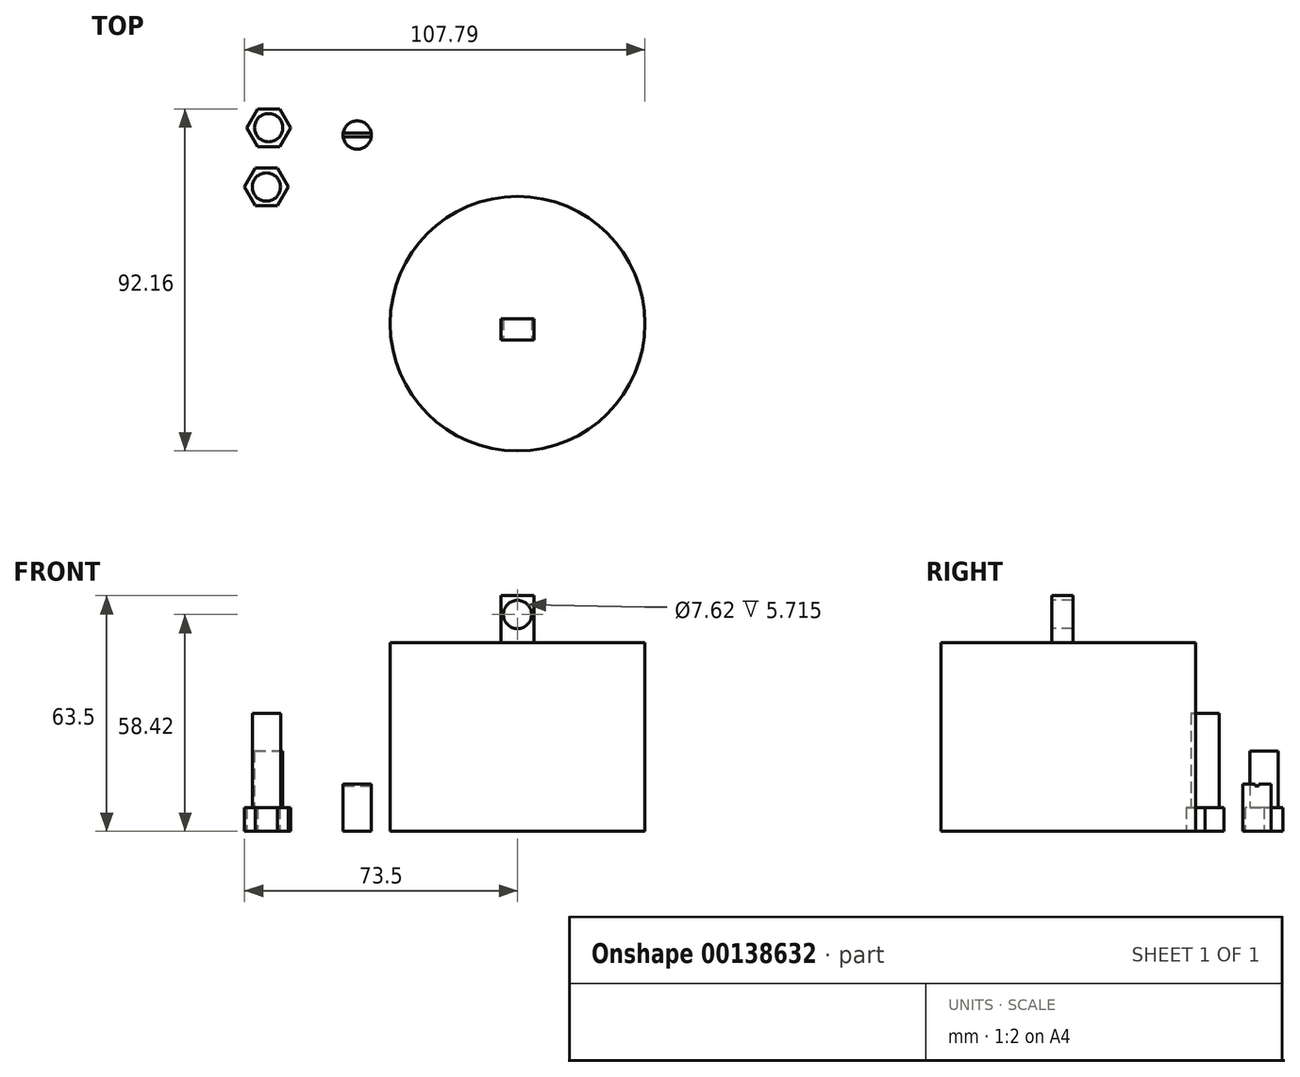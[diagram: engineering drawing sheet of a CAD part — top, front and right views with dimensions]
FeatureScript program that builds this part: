
annotation { "Feature Type Name" : "Feature", "Feature Type Description" : "" }
export const myFeature = defineFeature(function(context is Context, id is Id, definition is map)
    precondition{}
    {
        {
            var Q0;
            Q0=qCreatedBy(makeId("Top.planeOp"),FACE);
            var sketch = newSketch(context, id + "F0", { "sketchPlane" : qUnion([Q0])});
            skCircle(sketch, "E0", {"center": v(0, 0) * mm, "radius": 34.3 * mm});
            skSolve(sketch);
        }
        {
            var Q0;
            Q0 = qSketchRegion(id + "F0", true);
            extrude(context, id + "F1", {"entities" : qUnion([Q0]), "depth" : 50.8 * mm});
        }
        {
            var Q0;
            Q0=makeQuery(id+"F1.opExtrude","CAP_FACE",FACE,{"disambiguationData":[OSD([sQuery(id+"F0.wireOp",EDGE,"E0")])],"isStart":false});
            var sketch = newSketch(context, id + "F2", { "sketchPlane" : qUnion([Q0])});
            skLineSegment(sketch, "E1.top", {"start": v(-4.44, -4.45) * mm, "end": v(4.45, -4.45) * mm});
            skLineSegment(sketch, "E1.left", {"start": v(-4.45, 1.27) * mm, "end": v(-4.45, -4.45) * mm});
            skLineSegment(sketch, "E1.right", {"start": v(4.45, 1.27) * mm, "end": v(4.45, -4.45) * mm});
            skLineSegment(sketch, "E2", {"start": v(4.45, 1.27) * mm, "end": v(-4.45, 1.27) * mm});
            skSolve(sketch);
        }
        {
            var Q0;
            Q0 = qSketchRegion(id + "F2", true);
            extrude(context, id + "F3", {"entities" : qUnion([Q0]), "operationType" : NewBodyOperationType.ADD, "depth" : 12.7 * mm});
        }
        {
            var Q0;
            Q0=makeQuery(id+"F3.opExtrude","SWEPT_FACE",FACE,{"disambiguationData":[OSD([sQuery(id+"F2.wireOp",EDGE,"E1.top")])]});
            var sketch = newSketch(context, id + "F4", { "sketchPlane" : qUnion([Q0])});
            skCircle(sketch, "E3", {"center": v(0, 58.42) * mm, "radius": 3.81 * mm});
            skSolve(sketch);
        }
        {
            var Q0;
            Q0 = qSketchRegion(id + "F4", true);
            extrude(context, id + "F5", {"entities" : qUnion([Q0]), "operationType" : NewBodyOperationType.REMOVE, "oppositeDirection" : true, "depth" : 25.4 * mm});
        }
        {
            var Q0;
            Q0=qCreatedBy(makeId("Top.planeOp"),FACE);
            var sketch = newSketch(context, id + "F6", { "sketchPlane" : qUnion([Q0])});
            skCircle(sketch, "E4.cCircle", {"center": v(-67.01, 52.79) * mm, "radius": 5.08 * mm, "construction": true});
            skLineSegment(sketch, "E4.0", {"start": v(-64.08, 47.7) * mm, "end": v(-69.95, 47.7) * mm});
            skLineSegment(sketch, "E4.1", {"start": v(-69.95, 47.7) * mm, "end": v(-72.88, 52.79) * mm});
            skLineSegment(sketch, "E4.2", {"start": v(-72.88, 52.79) * mm, "end": v(-69.95, 57.87) * mm});
            skLineSegment(sketch, "E4.3", {"start": v(-69.95, 57.87) * mm, "end": v(-64.08, 57.87) * mm});
            skLineSegment(sketch, "E4.4", {"start": v(-64.08, 57.87) * mm, "end": v(-61.15, 52.79) * mm});
            skLineSegment(sketch, "E4.5", {"start": v(-61.15, 52.79) * mm, "end": v(-64.08, 47.7) * mm});
            skPoint(sketch, "E4.0.midPoint", {"position": v(-67.01, 47.7) * mm});
            skSolve(sketch);
        }
        {
            var Q0;
            Q0 = qSketchRegion(id + "F6", true);
            extrude(context, id + "F7", {"entities" : qUnion([Q0]), "depth" : 6.35 * mm});
        }
        {
            var Q0;
            Q0=makeQuery(id+"F7.opExtrude","CAP_FACE",FACE,{"disambiguationData":[OSD([sQuery(id+"F6.wireOp",EDGE,"E4.0"),sQuery(id+"F6.wireOp",EDGE,"E4.1"),sQuery(id+"F6.wireOp",EDGE,"E4.2"),sQuery(id+"F6.wireOp",EDGE,"E4.3"),sQuery(id+"F6.wireOp",EDGE,"E4.4"),sQuery(id+"F6.wireOp",EDGE,"E4.5")])],"isStart":false});
            var sketch = newSketch(context, id + "F8", { "sketchPlane" : qUnion([Q0])});
            skCircle(sketch, "E5.0", {"center": v(-67.01, 52.79) * mm, "radius": 3.8 * mm});
            skSolve(sketch);
        }
        {
            var Q0;
            Q0 = qSketchRegion(id + "F8", true);
            extrude(context, id + "F9", {"entities" : qUnion([Q0]), "operationType" : NewBodyOperationType.ADD, "depth" : 15.24 * mm});
        }
        {
            var Q0;
            Q0=qCreatedBy(makeId("Top.planeOp"),FACE);
            var sketch = newSketch(context, id + "F10", { "sketchPlane" : qUnion([Q0])});
            skCircle(sketch, "E6", {"center": v(-43.18, 50.8) * mm, "radius": 3.81 * mm});
            skSolve(sketch);
        }
        {
            var Q0;
            Q0 = qSketchRegion(id + "F10", true);
            extrude(context, id + "F11", {"entities" : qUnion([Q0]), "depth" : 12.7 * mm});
        }
        {
            var Q0;
            Q0=makeQuery(id+"F11.opExtrude","CAP_FACE",FACE,{"disambiguationData":[OSD([sQuery(id+"F10.wireOp",EDGE,"E6")])],"isStart":false});
            var sketch = newSketch(context, id + "F12", { "sketchPlane" : qUnion([Q0])});
            skLineSegment(sketch, "E7", {"start": v(-46.96, 50.3) * mm, "end": v(-39.4, 50.3) * mm});
            skArc(sketch, "E8", {"start": v(-39.4, 50.3) * mm, "mid": v(-39.37, 50.8) * mm, "end": v(-39.4, 51.3) * mm});
            skLineSegment(sketch, "E9", {"start": v(-39.4, 51.3) * mm, "end": v(-46.96, 51.3) * mm});
            skArc(sketch, "E10", {"start": v(-46.96, 51.3) * mm, "mid": v(-47, 50.8) * mm, "end": v(-46.96, 50.3) * mm});
            skSolve(sketch);
        }
        {
            var Q0;
            Q0 = qSketchRegion(id + "F12", true);
            extrude(context, id + "F13", {"entities" : qUnion([Q0]), "operationType" : NewBodyOperationType.REMOVE, "oppositeDirection" : true, "depth" : 0.5 * mm});
        }
        {
            var Q0;
            Q0=qCreatedBy(makeId("Top.planeOp"),FACE);
            var sketch = newSketch(context, id + "F14", { "sketchPlane" : qUnion([Q0])});
            skCircle(sketch, "E11.cCircle", {"center": v(-67.63, 36.8) * mm, "radius": 5.08 * mm, "construction": true});
            skLineSegment(sketch, "E11.0", {"start": v(-64.7, 31.73) * mm, "end": v(-70.56, 31.73) * mm});
            skLineSegment(sketch, "E11.1", {"start": v(-70.56, 31.73) * mm, "end": v(-73.5, 36.8) * mm});
            skLineSegment(sketch, "E11.2", {"start": v(-73.5, 36.8) * mm, "end": v(-70.56, 41.89) * mm});
            skLineSegment(sketch, "E11.3", {"start": v(-70.56, 41.89) * mm, "end": v(-64.7, 41.89) * mm});
            skLineSegment(sketch, "E11.4", {"start": v(-64.7, 41.89) * mm, "end": v(-61.77, 36.8) * mm});
            skLineSegment(sketch, "E11.5", {"start": v(-61.77, 36.8) * mm, "end": v(-64.7, 31.73) * mm});
            skPoint(sketch, "E11.0.midPoint", {"position": v(-67.63, 31.73) * mm});
            skSolve(sketch);
        }
        {
            var Q0;
            Q0 = qSketchRegion(id + "F14", true);
            extrude(context, id + "F15", {"entities" : qUnion([Q0]), "depth" : 6.35 * mm});
        }
        {
            var Q0;
            Q0=makeQuery(id+"F15.opExtrude","CAP_FACE",FACE,{"disambiguationData":[OSD([sQuery(id+"F14.wireOp",EDGE,"E11.0"),sQuery(id+"F14.wireOp",EDGE,"E11.1"),sQuery(id+"F14.wireOp",EDGE,"E11.2"),sQuery(id+"F14.wireOp",EDGE,"E11.3"),sQuery(id+"F14.wireOp",EDGE,"E11.4"),sQuery(id+"F14.wireOp",EDGE,"E11.5")])],"isStart":false});
            var sketch = newSketch(context, id + "F16", { "sketchPlane" : qUnion([Q0])});
            skCircle(sketch, "E12", {"center": v(-67.63, 36.8) * mm, "radius": 3.81 * mm});
            skSolve(sketch);
        }
        {
            var Q0;
            Q0 = qSketchRegion(id + "F16", true);
            extrude(context, id + "F17", {"entities" : qUnion([Q0]), "operationType" : NewBodyOperationType.ADD, "depth" : 25.4 * mm});
        }
    });
